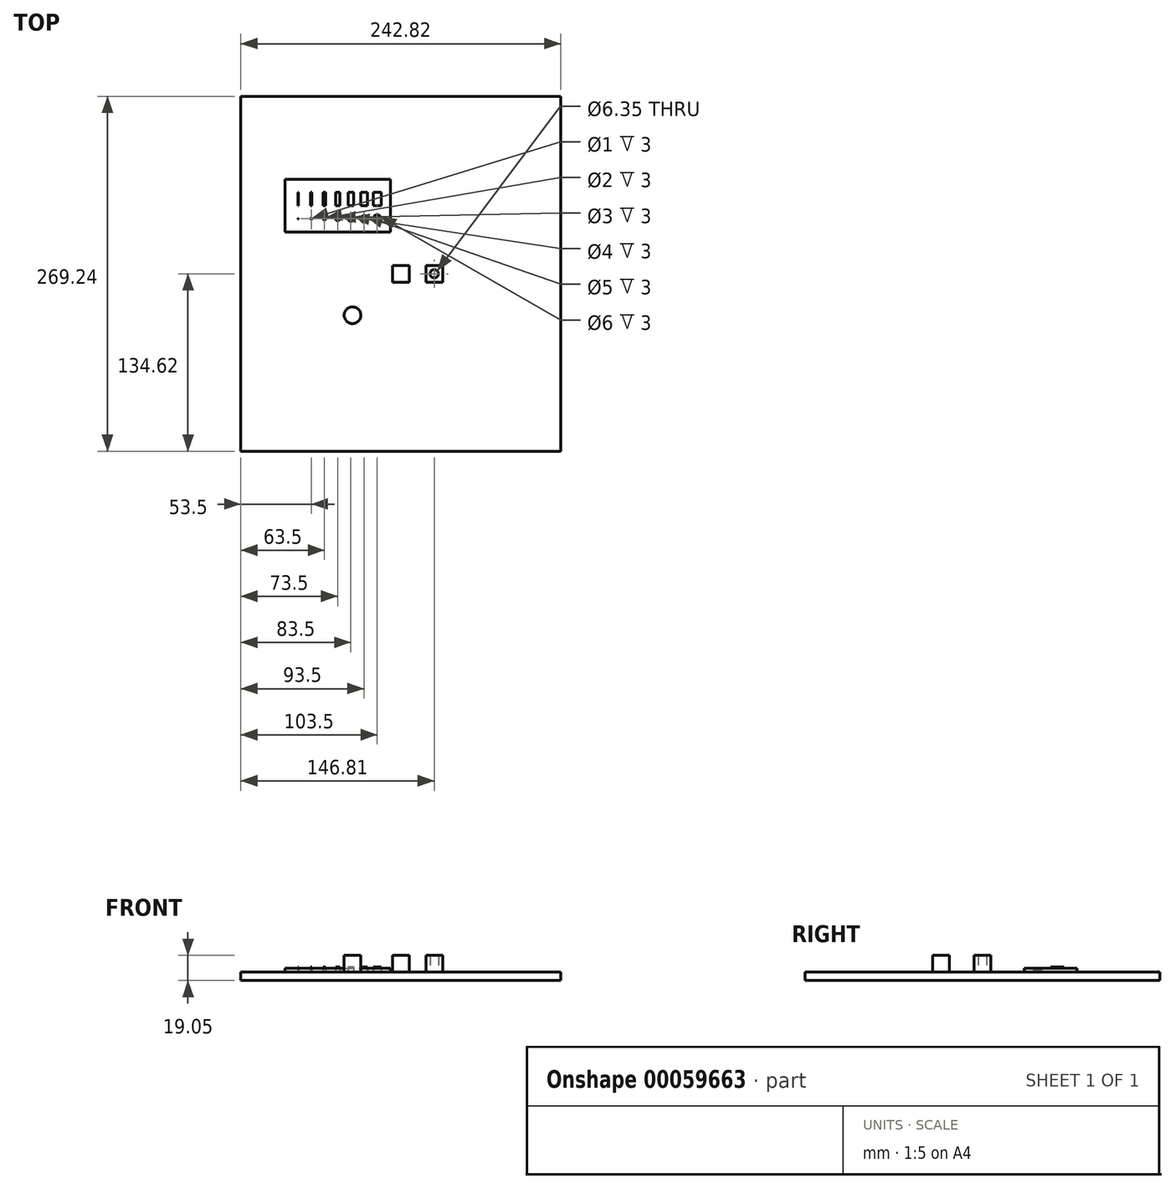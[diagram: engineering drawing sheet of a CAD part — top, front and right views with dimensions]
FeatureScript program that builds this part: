
annotation { "Feature Type Name" : "Feature", "Feature Type Description" : "" }
export const myFeature = defineFeature(function(context is Context, id is Id, definition is map)
    precondition{}
    {
        {
            var Q0;
            Q0=qCreatedBy(makeId("Top.planeOp"),FACE);
            var sketch = newSketch(context, id + "F0", { "sketchPlane" : qUnion([Q0])});
            skLineSegment(sketch, "E0.rect.bottom", {"start": v(121.41, -134.62) * mm, "end": v(-121.41, -134.62) * mm});
            skLineSegment(sketch, "E0.rect.top", {"start": v(121.41, 134.62) * mm, "end": v(-121.41, 134.62) * mm});
            skLineSegment(sketch, "E0.rect.left", {"start": v(121.41, -134.62) * mm, "end": v(121.41, 134.62) * mm});
            skLineSegment(sketch, "E0.rect.right", {"start": v(-121.41, -134.62) * mm, "end": v(-121.41, 134.62) * mm});
            skPoint(sketch, "E0.rect.middle", {"position": v(0, 0) * mm});
            skSolve(sketch);
        }
        {
            var Q0;
            Q0 = qSketchRegion(id + "F0", true);
            extrude(context, id + "F1", {"entities" : qUnion([Q0]), "depth" : 6.35 * mm});
        }
        {
            var Q0;
            Q0=makeQuery(id+"F1.opExtrude","CAP_FACE",FACE,{"disambiguationData":[OSD([sQuery(id+"F0.wireOp",EDGE,"E0.rect.bottom"),sQuery(id+"F0.wireOp",EDGE,"E0.rect.top"),sQuery(id+"F0.wireOp",EDGE,"E0.rect.left"),sQuery(id+"F0.wireOp",EDGE,"E0.rect.right")])],"isStart":false});
            var sketch = newSketch(context, id + "F2", { "sketchPlane" : qUnion([Q0])});
            skLineSegment(sketch, "E1.rect.bottom", {"start": v(6.35, -6.35) * mm, "end": v(-6.35, -6.35) * mm});
            skLineSegment(sketch, "E1.rect.top", {"start": v(6.35, 6.35) * mm, "end": v(-6.35, 6.35) * mm});
            skLineSegment(sketch, "E1.rect.left", {"start": v(6.35, -6.35) * mm, "end": v(6.35, 6.35) * mm});
            skLineSegment(sketch, "E1.rect.right", {"start": v(-6.35, -6.35) * mm, "end": v(-6.35, 6.35) * mm});
            skPoint(sketch, "E1.rect.middle", {"position": v(0, 0) * mm});
            skSolve(sketch);
        }
        {
            var Q0;
            Q0=makeQuery(id+"F2.imprint","IMPRINT",FACE,{"disambiguationData":[TD([[makeQuery(id+"F2.imprint","IMPRINT",EDGE,{"derivedFrom":sQuery(id+"F2.wireOp",EDGE,"E1.rect.bottom")}),-1.0]])]});
            extrude(context, id + "F3", {"entities" : qUnion([Q0]), "depth" : 12.7 * mm});
        }
        {
            var Q0;
            Q0=makeQuery(id+"F1.opExtrude","CAP_FACE",FACE,{"disambiguationData":[OSD([sQuery(id+"F0.wireOp",EDGE,"E0.rect.bottom"),sQuery(id+"F0.wireOp",EDGE,"E0.rect.top"),sQuery(id+"F0.wireOp",EDGE,"E0.rect.left"),sQuery(id+"F0.wireOp",EDGE,"E0.rect.right")])],"isStart":false});
            var sketch = newSketch(context, id + "F4", { "sketchPlane" : qUnion([Q0])});
            skLineSegment(sketch, "E2.rect.bottom", {"start": v(31.75, -6.35) * mm, "end": v(19.05, -6.35) * mm});
            skLineSegment(sketch, "E2.rect.top", {"start": v(31.75, 6.35) * mm, "end": v(19.05, 6.35) * mm});
            skLineSegment(sketch, "E2.rect.left", {"start": v(31.75, -6.35) * mm, "end": v(31.75, 6.35) * mm});
            skLineSegment(sketch, "E2.rect.right", {"start": v(19.05, -6.35) * mm, "end": v(19.05, 6.35) * mm});
            skPoint(sketch, "E2.rect.middle", {"position": v(25.4, 0) * mm});
            skCircle(sketch, "E3", {"center": v(25.4, 0) * mm, "radius": 3.18 * mm});
            skSolve(sketch);
        }
        {
            var Q0;
            Q0 = qSketchRegion(id + "F4", true);
            extrude(context, id + "F5", {"entities" : qUnion([Q0]), "depth" : 12.7 * mm});
        }
        {
            var Q0;
            Q0=makeQuery(id+"F1.opExtrude","CAP_FACE",FACE,{"disambiguationData":[OSD([sQuery(id+"F0.wireOp",EDGE,"E0.rect.bottom"),sQuery(id+"F0.wireOp",EDGE,"E0.rect.top"),sQuery(id+"F0.wireOp",EDGE,"E0.rect.left"),sQuery(id+"F0.wireOp",EDGE,"E0.rect.right")])],"isStart":false});
            var sketch = newSketch(context, id + "F6", { "sketchPlane" : qUnion([Q0])});
            skCircle(sketch, "E4", {"center": v(-36.68, -31.45) * mm, "radius": 6.35 * mm});
            skSolve(sketch);
        }
        {
            var Q0;
            Q0=makeQuery(id+"F6.imprint","IMPRINT",FACE,{"disambiguationData":[TD([[makeQuery(id+"F6.imprint","IMPRINT",EDGE,{"derivedFrom":sQuery(id+"F6.wireOp",EDGE,"E4")}),1.0]])]});
            extrude(context, id + "F7", {"entities" : qUnion([Q0]), "depth" : 12.7 * mm});
        }
        {
            var Q0;
            Q0=makeQuery(id+"F1.opExtrude","CAP_FACE",FACE,{"disambiguationData":[OSD([sQuery(id+"F0.wireOp",EDGE,"E0.rect.bottom"),sQuery(id+"F0.wireOp",EDGE,"E0.rect.top"),sQuery(id+"F0.wireOp",EDGE,"E0.rect.left"),sQuery(id+"F0.wireOp",EDGE,"E0.rect.right")])],"isStart":false});
            var sketch = newSketch(context, id + "F8", { "sketchPlane" : qUnion([Q0])});
            skLineSegment(sketch, "E5.bottom", {"start": v(-87.91, 71.7) * mm, "end": v(-7.91, 71.7) * mm});
            skLineSegment(sketch, "E5.top", {"start": v(-87.91, 31.7) * mm, "end": v(-7.91, 31.7) * mm});
            skLineSegment(sketch, "E5.left", {"start": v(-87.91, 71.7) * mm, "end": v(-87.91, 31.7) * mm});
            skLineSegment(sketch, "E5.right", {"start": v(-7.91, 71.7) * mm, "end": v(-7.91, 31.7) * mm});
            skLineSegment(sketch, "E6.rect.bottom", {"start": v(-77.66, 51.7) * mm, "end": v(-78.16, 51.7) * mm});
            skLineSegment(sketch, "E6.rect.top", {"start": v(-77.66, 61.7) * mm, "end": v(-78.16, 61.7) * mm});
            skLineSegment(sketch, "E6.rect.left", {"start": v(-77.66, 51.7) * mm, "end": v(-77.66, 61.7) * mm});
            skLineSegment(sketch, "E6.rect.right", {"start": v(-78.16, 51.7) * mm, "end": v(-78.16, 61.7) * mm});
            skPoint(sketch, "E6.rect.middle", {"position": v(-77.91, 56.7) * mm});
            skPoint(sketch, "E7.rect.middle", {"position": v(-67.91, 56.7) * mm});
            skLineSegment(sketch, "E7.rect.right", {"start": v(-68.41, 51.7) * mm, "end": v(-68.41, 61.7) * mm});
            skLineSegment(sketch, "E7.rect.left", {"start": v(-67.41, 51.7) * mm, "end": v(-67.41, 61.7) * mm});
            skLineSegment(sketch, "E7.rect.top", {"start": v(-67.41, 61.7) * mm, "end": v(-68.41, 61.7) * mm});
            skLineSegment(sketch, "E7.rect.bottom", {"start": v(-67.41, 51.7) * mm, "end": v(-68.41, 51.7) * mm});
            skPoint(sketch, "E8.rect.middle", {"position": v(-57.91, 56.7) * mm});
            skLineSegment(sketch, "E8.rect.right", {"start": v(-58.91, 51.7) * mm, "end": v(-58.91, 61.7) * mm});
            skLineSegment(sketch, "E8.rect.left", {"start": v(-56.91, 51.7) * mm, "end": v(-56.91, 61.7) * mm});
            skLineSegment(sketch, "E8.rect.top", {"start": v(-56.91, 61.7) * mm, "end": v(-58.91, 61.7) * mm});
            skLineSegment(sketch, "E8.rect.bottom", {"start": v(-56.91, 51.7) * mm, "end": v(-58.91, 51.7) * mm});
            skPoint(sketch, "E9.rect.middle", {"position": v(-47.91, 56.7) * mm});
            skLineSegment(sketch, "E9.rect.right", {"start": v(-49.41, 51.7) * mm, "end": v(-49.41, 61.7) * mm});
            skLineSegment(sketch, "E9.rect.left", {"start": v(-46.41, 51.7) * mm, "end": v(-46.41, 61.7) * mm});
            skLineSegment(sketch, "E9.rect.top", {"start": v(-46.41, 61.7) * mm, "end": v(-49.41, 61.7) * mm});
            skLineSegment(sketch, "E9.rect.bottom", {"start": v(-46.41, 51.7) * mm, "end": v(-49.41, 51.7) * mm});
            skPoint(sketch, "E10.rect.middle", {"position": v(-37.91, 56.7) * mm});
            skLineSegment(sketch, "E10.rect.right", {"start": v(-39.91, 51.7) * mm, "end": v(-39.91, 61.7) * mm});
            skLineSegment(sketch, "E10.rect.left", {"start": v(-35.91, 51.7) * mm, "end": v(-35.91, 61.7) * mm});
            skLineSegment(sketch, "E10.rect.top", {"start": v(-35.91, 61.7) * mm, "end": v(-39.91, 61.7) * mm});
            skLineSegment(sketch, "E10.rect.bottom", {"start": v(-35.91, 51.7) * mm, "end": v(-39.91, 51.7) * mm});
            skPoint(sketch, "E11.rect.middle", {"position": v(-27.91, 56.7) * mm});
            skLineSegment(sketch, "E11.rect.right", {"start": v(-30.41, 51.7) * mm, "end": v(-30.41, 61.7) * mm});
            skLineSegment(sketch, "E11.rect.left", {"start": v(-25.41, 51.7) * mm, "end": v(-25.41, 61.7) * mm});
            skLineSegment(sketch, "E11.rect.top", {"start": v(-25.41, 61.7) * mm, "end": v(-30.41, 61.7) * mm});
            skLineSegment(sketch, "E11.rect.bottom", {"start": v(-25.41, 51.7) * mm, "end": v(-30.41, 51.7) * mm});
            skPoint(sketch, "E12.rect.middle", {"position": v(-17.91, 56.7) * mm});
            skLineSegment(sketch, "E12.rect.right", {"start": v(-20.91, 51.7) * mm, "end": v(-20.91, 61.7) * mm});
            skLineSegment(sketch, "E12.rect.left", {"start": v(-14.91, 51.7) * mm, "end": v(-14.91, 61.7) * mm});
            skLineSegment(sketch, "E12.rect.top", {"start": v(-14.91, 61.7) * mm, "end": v(-20.91, 61.7) * mm});
            skLineSegment(sketch, "E12.rect.bottom", {"start": v(-14.91, 51.7) * mm, "end": v(-20.91, 51.7) * mm});
            skCircle(sketch, "E13", {"center": v(-77.91, 41.7) * mm, "radius": 0.25 * mm});
            skCircle(sketch, "E14", {"center": v(-67.91, 41.7) * mm, "radius": 0.5 * mm});
            skCircle(sketch, "E15", {"center": v(-57.91, 41.7) * mm, "radius": 1 * mm});
            skCircle(sketch, "E16", {"center": v(-47.91, 41.7) * mm, "radius": 1.5 * mm});
            skCircle(sketch, "E17", {"center": v(-37.91, 41.7) * mm, "radius": 2 * mm});
            skCircle(sketch, "E18", {"center": v(-27.91, 41.7) * mm, "radius": 2.5 * mm});
            skCircle(sketch, "E19", {"center": v(-17.91, 41.7) * mm, "radius": 3 * mm});
            skSolve(sketch);
        }
        {
            var Q0;
            Q0=makeQuery(id+"F8.imprint","IMPRINT",FACE,{"disambiguationData":[TD([[makeQuery(id+"F8.imprint","IMPRINT",EDGE,{"derivedFrom":sQuery(id+"F8.wireOp",EDGE,"E5.bottom")}),-1.0]])]});
            extrude(context, id + "F9", {"entities" : qUnion([Q0]), "depth" : 3 * mm});
        }
        {
            var Q0;
            Q0=makeQuery(id+"F8.imprint","IMPRINT",FACE,{"disambiguationData":[TD([[makeQuery(id+"F8.imprint","IMPRINT",EDGE,{"derivedFrom":sQuery(id+"F8.wireOp",EDGE,"E12.rect.right")}),-1.0]])]});
            var Q1;
            Q1=makeQuery(id+"F8.imprint","IMPRINT",FACE,{"disambiguationData":[TD([[makeQuery(id+"F8.imprint","IMPRINT",EDGE,{"derivedFrom":sQuery(id+"F8.wireOp",EDGE,"E11.rect.right")}),-1.0]])]});
            var Q2;
            Q2=makeQuery(id+"F8.imprint","IMPRINT",FACE,{"disambiguationData":[TD([[makeQuery(id+"F8.imprint","IMPRINT",EDGE,{"derivedFrom":sQuery(id+"F8.wireOp",EDGE,"E10.rect.right")}),-1.0]])]});
            var Q3;
            Q3=makeQuery(id+"F8.imprint","IMPRINT",FACE,{"disambiguationData":[TD([[makeQuery(id+"F8.imprint","IMPRINT",EDGE,{"derivedFrom":sQuery(id+"F8.wireOp",EDGE,"E9.rect.right")}),-1.0]])]});
            var Q4;
            Q4=makeQuery(id+"F8.imprint","IMPRINT",FACE,{"disambiguationData":[TD([[makeQuery(id+"F8.imprint","IMPRINT",EDGE,{"derivedFrom":sQuery(id+"F8.wireOp",EDGE,"E8.rect.right")}),-1.0]])]});
            var Q5;
            Q5=makeQuery(id+"F8.imprint","IMPRINT",FACE,{"disambiguationData":[TD([[makeQuery(id+"F8.imprint","IMPRINT",EDGE,{"derivedFrom":sQuery(id+"F8.wireOp",EDGE,"E7.rect.right")}),-1.0]])]});
            var Q6;
            Q6=makeQuery(id+"F8.imprint","IMPRINT",FACE,{"disambiguationData":[TD([[makeQuery(id+"F8.imprint","IMPRINT",EDGE,{"derivedFrom":sQuery(id+"F8.wireOp",EDGE,"E6.rect.bottom")}),-1.0]])]});
            extrude(context, id + "F10", {"entities" : qUnion([Q0, Q1, Q2, Q3, Q4, Q5, Q6]), "operationType" : NewBodyOperationType.ADD, "depth" : 4 * mm});
        }
    });
